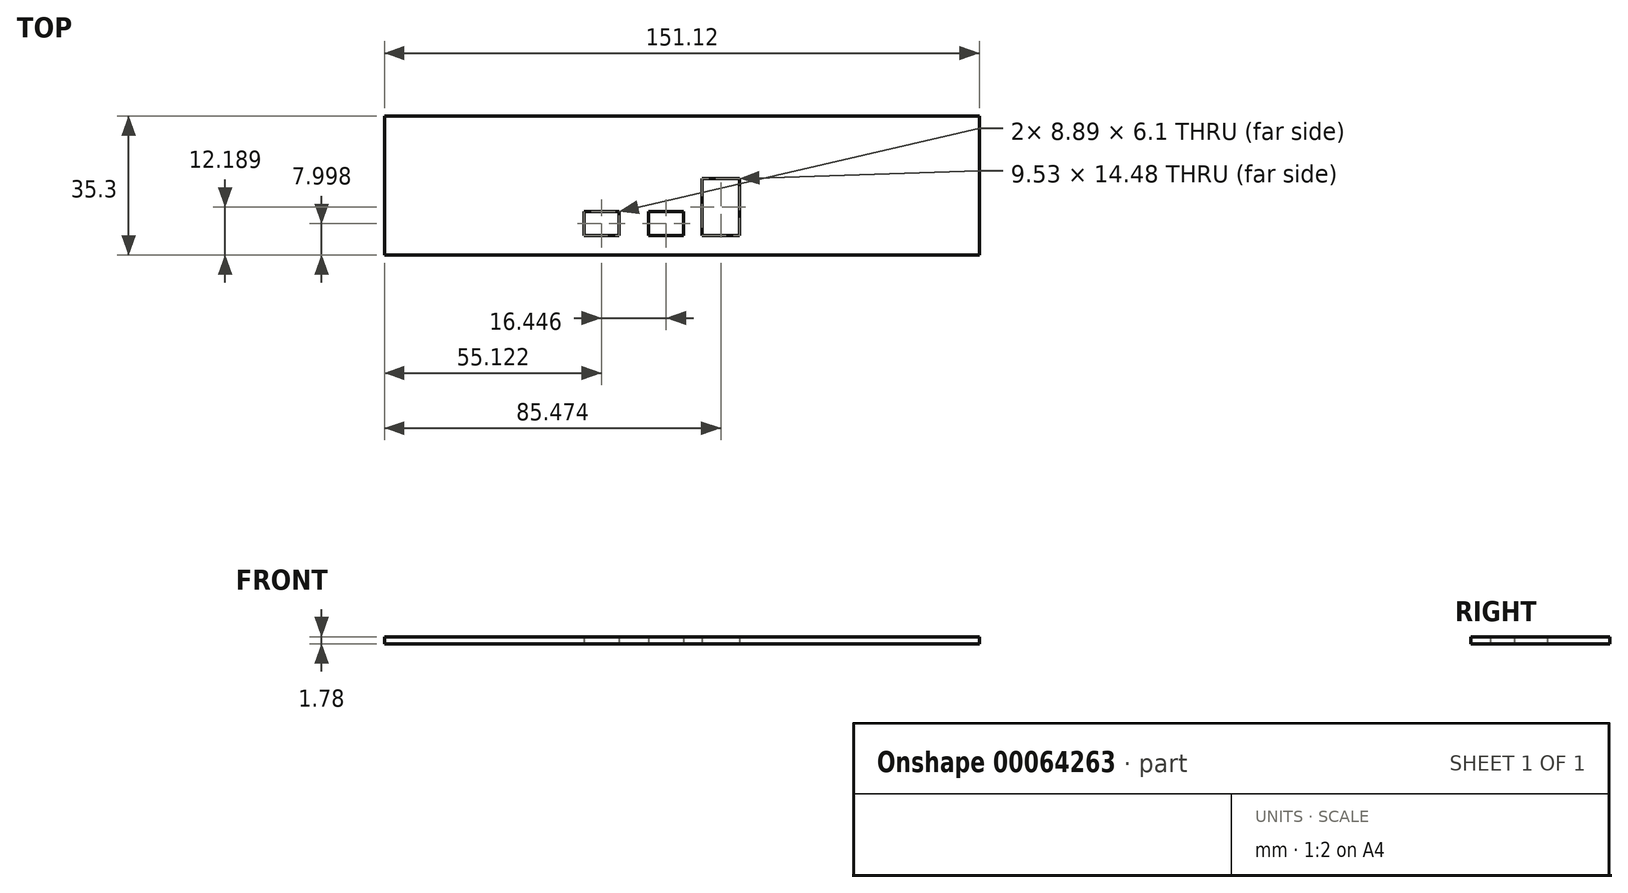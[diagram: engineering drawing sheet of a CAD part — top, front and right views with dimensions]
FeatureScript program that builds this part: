
annotation { "Feature Type Name" : "Feature", "Feature Type Description" : "" }
export const myFeature = defineFeature(function(context is Context, id is Id, definition is map)
    precondition{}
    {
        {
            var Q0;
            Q0=qCreatedBy(makeId("Top.planeOp"),FACE);
            var sketch = newSketch(context, id + "F0", { "sketchPlane" : qUnion([Q0])});
            skLineSegment(sketch, "E0.bottom", {"start": v(-76.39, -103.26) * mm, "end": v(74.74, -103.26) * mm});
            skLineSegment(sketch, "E0.top", {"start": v(-76.39, -138.57) * mm, "end": v(74.74, -138.57) * mm});
            skLineSegment(sketch, "E0.left", {"start": v(-76.39, -103.26) * mm, "end": v(-76.39, -138.57) * mm});
            skLineSegment(sketch, "E0.right", {"start": v(74.74, -103.26) * mm, "end": v(74.74, -138.57) * mm});
            skSolve(sketch);
        }
        {
            var Q0;
            Q0=qSketchRegion(id+"F0",true);
            extrude(context, id + "F1", {"entities" : qUnion([Q0]), "depth" : 1.78 * mm, "offsetDistance" : 25.4 * mm});
        }
        {
            var Q0;
            Q0=qCreatedBy(makeId("Top.planeOp"),FACE);
            var sketch = newSketch(context, id + "F2", { "sketchPlane" : qUnion([Q0])});
            skLineSegment(sketch, "E1.bottom", {"start": v(-75.56, 17.65) * mm, "end": v(75.57, 17.65) * mm});
            skLineSegment(sketch, "E1.top", {"start": v(-75.56, -17.65) * mm, "end": v(75.57, -17.65) * mm});
            skLineSegment(sketch, "E1.left", {"start": v(-75.56, 17.65) * mm, "end": v(-75.56, -17.65) * mm});
            skLineSegment(sketch, "E1.right", {"start": v(75.57, 17.65) * mm, "end": v(75.57, -17.65) * mm});
            skSolve(sketch);
        }
        {
            var Q0;
            Q0=makeQuery(id+"F2.imprint","IMPRINT",FACE,{"disambiguationData":[TD([[makeQuery(id+"F2.imprint","IMPRINT",EDGE,{"derivedFrom":sQuery(id+"F2.wireOp",EDGE,"E1.bottom")}),-1.0]])]});
            var sketch = newSketch(context, id + "F3", { "sketchPlane" : qUnion([Q0])});
            skLineSegment(sketch, "E2", {"start": v(-75.56, 0.13) * mm, "end": v(75.57, 0.13) * mm, "construction": true});
            skLineSegment(sketch, "E3", {"start": v(-75.56, -8.64) * mm, "end": v(75.57, -8.64) * mm, "construction": true});
            skLineSegment(sketch, "E4", {"start": v(-75.56, -12.7) * mm, "end": v(75.57, -12.7) * mm, "construction": true});
            skLineSegment(sketch, "E5", {"start": v(-36.45, 17.65) * mm, "end": v(-36.45, -17.65) * mm, "construction": true});
            skLineSegment(sketch, "E6", {"start": v(0.45, -6.6) * mm, "end": v(0.45, -12.7) * mm});
            skLineSegment(sketch, "E7", {"start": v(0.45, -12.7) * mm, "end": v(-8.44, -12.7) * mm});
            skLineSegment(sketch, "E8", {"start": v(-8.44, -12.7) * mm, "end": v(-8.44, -6.6) * mm});
            skLineSegment(sketch, "E9", {"start": v(-16, -6.6) * mm, "end": v(-16, -12.7) * mm});
            skLineSegment(sketch, "E10", {"start": v(-16, -12.7) * mm, "end": v(-24.88, -12.7) * mm});
            skLineSegment(sketch, "E11", {"start": v(-24.88, -12.7) * mm, "end": v(-24.88, -6.6) * mm});
            skLineSegment(sketch, "E12", {"start": v(-24.88, -6.6) * mm, "end": v(-16, -6.6) * mm});
            skLineSegment(sketch, "E13", {"start": v(-8.44, -6.6) * mm, "end": v(0.45, -6.6) * mm});
            skLineSegment(sketch, "E14", {"start": v(14.68, 1.78) * mm, "end": v(14.68, -12.7) * mm});
            skLineSegment(sketch, "E15", {"start": v(5.15, -12.7) * mm, "end": v(14.68, -12.7) * mm});
            skLineSegment(sketch, "E16", {"start": v(5.15, -12.7) * mm, "end": v(5.15, 1.78) * mm});
            skLineSegment(sketch, "E17", {"start": v(5.15, 1.78) * mm, "end": v(14.68, 1.78) * mm});
            skSolve(sketch);
        }
        {
            var Q0;
            Q0=qSketchRegion(id+"F2",true);
            extrude(context, id + "F4", {"entities" : qUnion([Q0]), "depth" : 1.78 * mm, "offsetDistance" : 25.4 * mm});
        }
        {
            var Q0;
            Q0=qSketchRegion(id+"F3",true);
            extrude(context, id + "F5", {"entities" : qUnion([Q0]), "operationType" : NewBodyOperationType.REMOVE, "depth" : 2.54 * mm, "offsetDistance" : 25.4 * mm});
        }
        {
            var Q0;
            Q0=makeQuery(id+"F1.opExtrude","SWEPT_BODY",BODY,{"disambiguationData":[OSD([sQuery(id+"F0.wireOp",EDGE,"E0.bottom"),sQuery(id+"F0.wireOp",EDGE,"E0.top"),sQuery(id+"F0.wireOp",EDGE,"E0.left"),sQuery(id+"F0.wireOp",EDGE,"E0.right")])]});
            deleteBodies(context, id + "F6", {"entities" : qUnion([Q0])});
        }
    });
